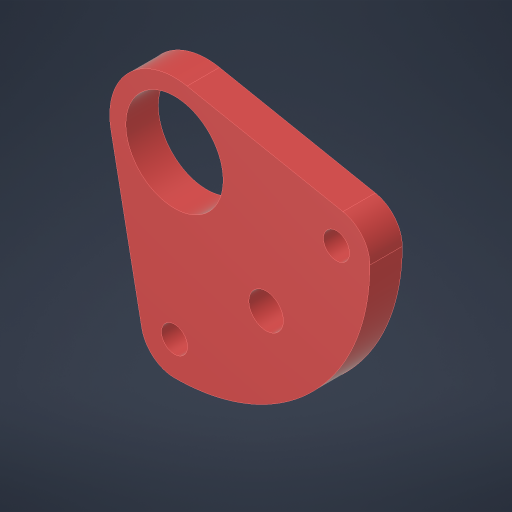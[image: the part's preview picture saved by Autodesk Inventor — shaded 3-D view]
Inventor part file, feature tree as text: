
AUTODESK INVENTOR PART (.ipt)
format: ipt  version: 2023.4 (Build 274418000, 418)  size: 240,640 bytes
history: native  units: in
note: dims shown in document units (in); Inventor stores cm internally (conversion verified against a paired STEP export)
features: sketch x2, extrude x2, hole x2, projected_geometry x1
ambient origin geometry x8: Origin, YZ Plane, XZ Plane, XY Plane, X Axis, Y Axis, Z Axis, Center Point
bodies: Solid1 (feature_tree)
feature tree (7):
  sketch  "Sketch1"  dims[d0=2.5in d1=0.88in]
  extrude  "Extrusion1"  Depth=0.88in
  hole  "Hole1"  [1 undecoded]
  extrude  "Extrusion2"  Depth=0.375in
  hole  "Hole2"  [1 undecoded]
  sketch  "Sketch2"  dims[d3=1.0in d4=45.0deg d5=0.5157in d6=0.5157in d7=0.5157in d8=0.5157in d9=0.5157in d10=0.2579in d11=0.5157in d12=0.25in d13=0.0in d14=0.2657in d15=0.38in d16=0.119in d17=0.25in d18=0.5635in d19=0.375in d20=0.0in d23=0.125in d24=0.75in d25=0.25in d26=0.0in d27=0.201in d28=0.75in d29=0.385in d30=0.25in d31=0.5635in d32=0.375in d33=0.0in]
  projected_geometry  "Project Cut Edges1"
note: 2 required parameter values undecoded (feature->parameter linkage not recoverable at this tier; creation-order binding heuristic only, values carry confidence <= 0.55)
